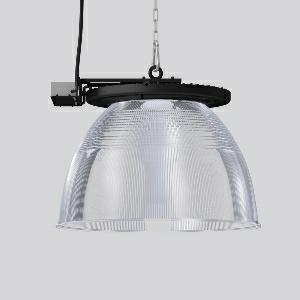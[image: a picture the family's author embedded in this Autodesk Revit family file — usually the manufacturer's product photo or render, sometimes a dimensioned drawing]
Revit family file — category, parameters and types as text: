
# Revit family: industrial_hall_refraktor_921712_003_1cc3
name_source: partatom
category: Lighting Fixtures
units: mm (PartAtom-declared; Revit-internal decimal feet)

## family parameters
Cut with Voids When Loaded = No
Host = Face
Light Source = No
Part Type = Normal
Room Calculation Point = No
Round Connector Dimension = Use Diameter
Shared = No

## types (1)
- INDUSTRIAL HALL refraktor (1 x LED Modul 840, 18600 lm, 4000)
    Apparent Load = 150 VA
    CIE Flux Codes = 84 94 98 93 100
    Color Rendering = 80
    Color Temperature = 4000
    Default Elevation = 1800 mm
    Description = Series: INDUSTRIAL HALL
Round highbay luminaire for high ambient temperatures. Robust housing made of die-cast aluminium with eye ring, powder coated. Vertical cooling ribs ensure constant heat dissipation for optimal thermal management. Diffuser made of clear, non-reflecting, single pane safety glass (toughened glass). Refractor: PMMA, transparent. Primary light control with high-performance wide-area LEDs and reflector made of plastic (PMMA) for optimum glare limitation: RUG <19. Easy to install thanks to 1-point suspension. Suitable for chain or steel cable suspension (to be provided on site). Ceiling- and wall-mounting bracket available as accessory. Luminaire with limited surface temperature in accordance with EN 60598-2-24 for use in environments in which a deposit of conductive dust on the luminaire can be expected. Qualified for use in the food and drink industry. 
Colour: deep black, matt (RAL 9005)
Length: 581 mm
Width: 570 mm
Height: 461 mm
Lamp: LED
Socket: without socket
Colour temperature: 4000K
Colour rendering index (CRI): 80
System power: 150 W
Rated luminous flux: 18600 lm
Luminous efficiency: 124 lm/W
Control gear: Regulated power supply
Protection class: I
Type of protection: IP 65
    Height = 461 mm
    Lamp = 1 x LED Modul 840
    Lamp Light Flux = 18600 lm
    Lamp count = 1
    Length = 581 mm
    Lifetime = 50000 h
    Luminous efficacy = 124 lm/W
    Manufacturer = RZB
    ModVariant = No
    Model = 921712.003
    Mounting Place = Ceiling
    Mounting Type = Pendant
    Number of Poles = 1
    OnlyDefault = Yes
    Power Factor = 1
    Product Name = INDUSTRIAL HALL refraktor
    Product group = Pendant commercial luminaires
    ProductGroupID = 903
    Protection Class = Protection class I
    Protection Degree = Degree of protection
    RLX_Detail_Level = 1
    RLX_Emergency_Light_Flux = 0 lm
    RLX_Emergency_Type = 0
    RLX_Emergency_Type_DB = No
    RlxData = <blob elided: 238673 chars, md5=c0cbbdbf>
    Socket = socket
    Standby Power = 0 W
    System Light Flux = 18600 lm
    System Power = 150 W
    Type Comments = Product without accessories
    Type Image = 921712.003.jpg
    URL = http://relux.com
    VarID = ---
    Voltage = 0 V
    Weight = 0.00 kg
    Width = 570 mm

## geometry (parser evidence)
native form markers: Blend x4, Sweep x12
no freeform markers — native parametric forms only
